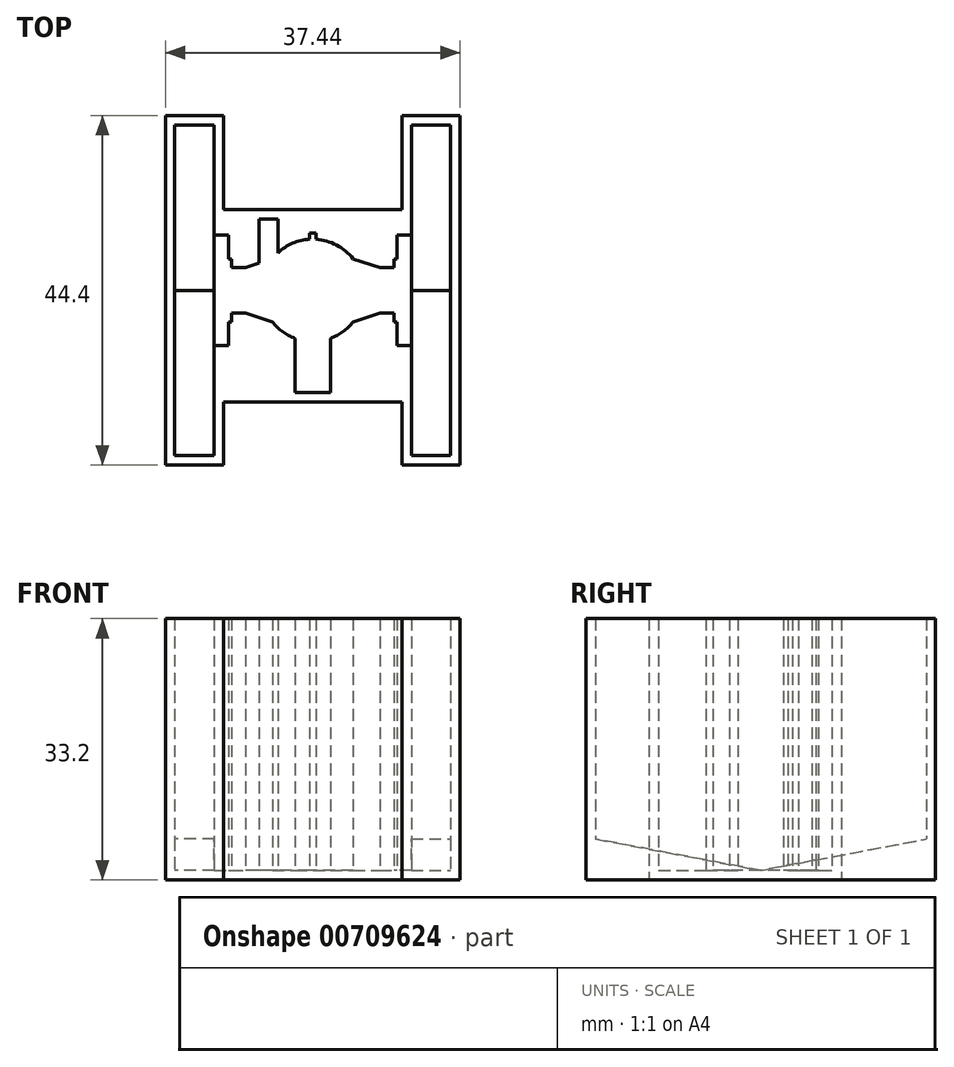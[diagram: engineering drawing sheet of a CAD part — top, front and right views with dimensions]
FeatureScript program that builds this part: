
annotation { "Feature Type Name" : "Feature", "Feature Type Description" : "" }
export const myFeature = defineFeature(function(context is Context, id is Id, definition is map)
    precondition{}
    {
        {
            var Q0;
            Q0=qCreatedBy(makeId("Top.planeOp"),FACE);
            var sketch = newSketch(context, id + "F0", { "sketchPlane" : qUnion([Q0])});
            skArc(sketch, "E0", {"start": v(-5.12, -4) * mm, "mid": v(-3.83, -5.25) * mm, "end": v(-2.25, -6.1) * mm});
            skLineSegment(sketch, "E1.bottom", {"start": v(12.52, 21) * mm, "end": v(12.52, 7) * mm});
            skLineSegment(sketch, "E1.left", {"start": v(12.52, 21) * mm, "end": v(17.52, 21) * mm});
            skLineSegment(sketch, "E1.right", {"start": v(12.52, -21) * mm, "end": v(17.52, -21) * mm});
            skLineSegment(sketch, "E2.left", {"start": v(8.52, 2.9) * mm, "end": v(10.32, 2.9) * mm});
            skLineSegment(sketch, "E3", {"start": v(8.52, 2.9) * mm, "end": v(8.52, 4) * mm, "construction": true});
            skLineSegment(sketch, "E4", {"start": v(8.52, 4) * mm, "end": v(5.12, 4) * mm, "construction": true});
            skLineSegment(sketch, "E5", {"start": v(5.12, 4) * mm, "end": v(8.52, 2.9) * mm});
            skLineSegment(sketch, "E6", {"start": v(17.52, 21) * mm, "end": v(17.52, 0) * mm});
            skLineSegment(sketch, "E7.MirrorCS", {"start": v(5.12, -4) * mm, "end": v(8.52, -2.9) * mm});
            skLineSegment(sketch, "E8.MirrorCS", {"start": v(8.52, -2.9) * mm, "end": v(10.32, -2.9) * mm});
            skLineSegment(sketch, "E9.MirrorCS", {"start": v(17.52, -21) * mm, "end": v(17.52, 0) * mm});
            skLineSegment(sketch, "E10", {"start": v(0, 29.44) * mm, "end": v(0, 7.3) * mm, "construction": true});
            skLineSegment(sketch, "E11.MirrorCS", {"start": v(-8.52, -2.9) * mm, "end": v(-10.32, -2.9) * mm});
            skLineSegment(sketch, "E12.MirrorCS", {"start": v(-12.52, -21) * mm, "end": v(-17.52, -21) * mm});
            skLineSegment(sketch, "E13.MirrorCS", {"start": v(-6.82, 3.45) * mm, "end": v(-8.52, 2.9) * mm});
            skLineSegment(sketch, "E14.MirrorCS", {"start": v(33.28, 0) * mm, "end": v(-32.9, 0) * mm, "construction": true});
            skLineSegment(sketch, "E15.MirrorCS", {"start": v(-5.12, -4) * mm, "end": v(-8.52, -2.9) * mm});
            skLineSegment(sketch, "E16.MirrorCS", {"start": v(-17.52, 21) * mm, "end": v(-17.52, 0) * mm});
            skLineSegment(sketch, "E17.MirrorCS", {"start": v(-12.52, 21) * mm, "end": v(-17.52, 21) * mm});
            skArc(sketch, "E18.MirrorC", {"start": v(-4.42, 4.76) * mm, "mid": v(-2.56, 5.97) * mm, "end": v(-0.4, 6.49) * mm});
            skLineSegment(sketch, "E19.MirrorCS", {"start": v(-17.52, -21) * mm, "end": v(-17.52, 0) * mm});
            skLineSegment(sketch, "E20", {"start": v(-6.82, 3.45) * mm, "end": v(-6.82, 9.06) * mm});
            skLineSegment(sketch, "E21", {"start": v(-4.42, 4.76) * mm, "end": v(-4.42, 9.06) * mm});
            skLineSegment(sketch, "E22", {"start": v(-4.42, 9.06) * mm, "end": v(-6.82, 9.06) * mm});
            skArc(sketch, "E23.trimOffspring", {"start": v(5.12, 4) * mm, "mid": v(3.03, 5.75) * mm, "end": v(0.4, 6.49) * mm});
            skArc(sketch, "E24.trimOffspring", {"start": v(5.12, -4) * mm, "mid": v(3.83, -5.25) * mm, "end": v(2.25, -6.1) * mm});
            skLineSegment(sketch, "E25", {"start": v(10.72, 4) * mm, "end": v(10.32, 4) * mm});
            skLineSegment(sketch, "E26", {"start": v(10.32, 4) * mm, "end": v(10.32, 2.9) * mm});
            skLineSegment(sketch, "E27.MirrorCS", {"start": v(10.32, -4) * mm, "end": v(10.32, -2.9) * mm});
            skLineSegment(sketch, "E28.MirrorCS", {"start": v(-10.32, 4) * mm, "end": v(-10.32, 2.9) * mm});
            skLineSegment(sketch, "E29.MirrorCS", {"start": v(-10.32, -4) * mm, "end": v(-10.32, -2.9) * mm});
            skLineSegment(sketch, "E30", {"start": v(-10.32, 2.9) * mm, "end": v(-8.52, 2.9) * mm});
            skLineSegment(sketch, "E31", {"start": v(0, 0) * mm, "end": v(0, -13) * mm, "construction": true});
            skLineSegment(sketch, "E32", {"start": v(-2.25, -13) * mm, "end": v(2.25, -13) * mm});
            skLineSegment(sketch, "E33", {"start": v(-2.25, -13) * mm, "end": v(-2.25, -6.1) * mm});
            skLineSegment(sketch, "E34", {"start": v(2.25, -13) * mm, "end": v(2.25, -6.1) * mm});
            skArc(sketch, "E35.trimOffspring", {"start": v(-2.25, -6.1) * mm, "mid": v(-3.83, -5.25) * mm, "end": v(-5.12, -4) * mm});
            skLineSegment(sketch, "E36", {"start": v(0, 7.3) * mm, "end": v(0.4, 7.3) * mm});
            skLineSegment(sketch, "E37", {"start": v(0.4, 7.3) * mm, "end": v(0.4, 6.49) * mm});
            skLineSegment(sketch, "E38", {"start": v(0, 7.3) * mm, "end": v(-0.4, 7.3) * mm});
            skLineSegment(sketch, "E39", {"start": v(-0.4, 7.3) * mm, "end": v(-0.4, 6.49) * mm});
            skLineSegment(sketch, "E40.trimOffspring", {"start": v(0, 6.5) * mm, "end": v(0, -27.69) * mm, "construction": true});
            skArc(sketch, "E41.trimOffspring", {"start": v(0.4, 6.49) * mm, "mid": v(3.03, 5.75) * mm, "end": v(5.12, 4) * mm});
            skArc(sketch, "E42.trimOffspring", {"start": v(-0.4, 6.49) * mm, "mid": v(-2.56, 5.97) * mm, "end": v(-4.42, 4.76) * mm});
            skLineSegment(sketch, "E43.MirrorCS", {"start": v(10.72, -4) * mm, "end": v(10.32, -4) * mm});
            skLineSegment(sketch, "E44.MirrorCS", {"start": v(-10.72, -4) * mm, "end": v(-10.32, -4) * mm});
            skLineSegment(sketch, "E45.MirrorCS", {"start": v(-10.72, 4) * mm, "end": v(-10.32, 4) * mm});
            skLineSegment(sketch, "E46", {"start": v(12.52, 7) * mm, "end": v(10.72, 7) * mm});
            skLineSegment(sketch, "E47", {"start": v(10.72, 7) * mm, "end": v(10.72, 4) * mm});
            skLineSegment(sketch, "E48.MirrorCS", {"start": v(12.52, -21) * mm, "end": v(12.52, -7) * mm});
            skLineSegment(sketch, "E49.MirrorCS", {"start": v(10.72, -7) * mm, "end": v(10.72, -4) * mm});
            skLineSegment(sketch, "E50.MirrorCS", {"start": v(12.52, -7) * mm, "end": v(10.72, -7) * mm});
            skLineSegment(sketch, "E51.MirrorCS", {"start": v(-12.52, -21) * mm, "end": v(-12.52, -7) * mm});
            skLineSegment(sketch, "E52.MirrorCS", {"start": v(-12.52, -7) * mm, "end": v(-10.72, -7) * mm});
            skLineSegment(sketch, "E53.MirrorCS", {"start": v(-10.72, -7) * mm, "end": v(-10.72, -4) * mm});
            skLineSegment(sketch, "E54.MirrorCS", {"start": v(-10.72, 7) * mm, "end": v(-10.72, 4) * mm});
            skLineSegment(sketch, "E55.MirrorCS", {"start": v(-12.52, 21) * mm, "end": v(-12.52, 7) * mm});
            skLineSegment(sketch, "E56.MirrorCS", {"start": v(-12.52, 7) * mm, "end": v(-10.72, 7) * mm});
            skArc(sketch, "E57", {"start": v(-19.07, 82.73) * mm, "mid": v(-17.82, 84.02) * mm, "end": v(-16.97, 85.6) * mm});
            skLineSegment(sketch, "E58.bottom", {"start": v(-44.07, 100.38) * mm, "end": v(-30.07, 100.38) * mm});
            skLineSegment(sketch, "E58.left", {"start": v(-44.07, 100.38) * mm, "end": v(-44.07, 105.38) * mm});
            skLineSegment(sketch, "E58.right", {"start": v(-2.07, 100.38) * mm, "end": v(-2.07, 105.38) * mm});
            skLineSegment(sketch, "E59.left", {"start": v(-25.97, 96.38) * mm, "end": v(-25.97, 98.18) * mm});
            skLineSegment(sketch, "E60", {"start": v(-25.97, 96.38) * mm, "end": v(-27.07, 96.38) * mm, "construction": true});
            skLineSegment(sketch, "E61", {"start": v(-27.07, 96.38) * mm, "end": v(-27.07, 92.98) * mm, "construction": true});
            skLineSegment(sketch, "E62", {"start": v(-27.07, 92.98) * mm, "end": v(-25.97, 96.38) * mm});
            skLineSegment(sketch, "E63", {"start": v(-44.07, 105.38) * mm, "end": v(-23.07, 105.38) * mm});
            skLineSegment(sketch, "E64.MirrorCS", {"start": v(-19.07, 92.98) * mm, "end": v(-20.17, 96.38) * mm});
            skLineSegment(sketch, "E65.MirrorCS", {"start": v(-20.17, 96.38) * mm, "end": v(-20.17, 98.18) * mm});
            skLineSegment(sketch, "E66.MirrorCS", {"start": v(-2.07, 105.38) * mm, "end": v(-23.07, 105.38) * mm});
            skLineSegment(sketch, "E67.MirrorCS", {"start": v(-20.17, 79.33) * mm, "end": v(-20.17, 77.53) * mm});
            skLineSegment(sketch, "E68.MirrorCS", {"start": v(-2.07, 75.33) * mm, "end": v(-2.07, 70.33) * mm});
            skLineSegment(sketch, "E69.MirrorCS", {"start": v(-26.52, 81.03) * mm, "end": v(-25.97, 79.33) * mm});
            skLineSegment(sketch, "E70.MirrorCS", {"start": v(-19.07, 82.73) * mm, "end": v(-20.17, 79.33) * mm});
            skLineSegment(sketch, "E71.MirrorCS", {"start": v(-44.07, 70.33) * mm, "end": v(-23.07, 70.33) * mm});
            skLineSegment(sketch, "E72.MirrorCS", {"start": v(-44.07, 75.33) * mm, "end": v(-44.07, 70.33) * mm});
            skArc(sketch, "E73.MirrorC", {"start": v(-27.83, 83.43) * mm, "mid": v(-29.04, 85.3) * mm, "end": v(-29.55, 87.45) * mm});
            skLineSegment(sketch, "E74.MirrorCS", {"start": v(-2.07, 70.33) * mm, "end": v(-23.07, 70.33) * mm});
            skLineSegment(sketch, "E75", {"start": v(-26.52, 81.03) * mm, "end": v(-32.13, 81.03) * mm});
            skLineSegment(sketch, "E76", {"start": v(-27.83, 83.43) * mm, "end": v(-32.13, 83.43) * mm});
            skLineSegment(sketch, "E77", {"start": v(-32.13, 83.43) * mm, "end": v(-32.13, 81.03) * mm});
            skArc(sketch, "E78.trimOffspring", {"start": v(-27.07, 92.98) * mm, "mid": v(-28.82, 90.88) * mm, "end": v(-29.55, 88.25) * mm});
            skArc(sketch, "E79.trimOffspring", {"start": v(-19.07, 92.98) * mm, "mid": v(-17.82, 91.69) * mm, "end": v(-16.97, 90.1) * mm});
            skLineSegment(sketch, "E80", {"start": v(-27.07, 98.58) * mm, "end": v(-27.07, 98.18) * mm});
            skLineSegment(sketch, "E81", {"start": v(-27.07, 98.18) * mm, "end": v(-25.97, 98.18) * mm});
            skLineSegment(sketch, "E82.MirrorCS", {"start": v(-19.07, 98.18) * mm, "end": v(-20.17, 98.18) * mm});
            skLineSegment(sketch, "E83.MirrorCS", {"start": v(-27.07, 77.53) * mm, "end": v(-25.97, 77.53) * mm});
            skLineSegment(sketch, "E84.MirrorCS", {"start": v(-19.07, 77.53) * mm, "end": v(-20.17, 77.53) * mm});
            skLineSegment(sketch, "E85", {"start": v(-25.97, 77.53) * mm, "end": v(-25.97, 79.33) * mm});
            skLineSegment(sketch, "E86", {"start": v(-23.07, 87.85) * mm, "end": v(-10.07, 87.85) * mm, "construction": true});
            skLineSegment(sketch, "E87", {"start": v(-10.07, 85.6) * mm, "end": v(-10.07, 90.1) * mm});
            skLineSegment(sketch, "E88", {"start": v(-10.07, 85.6) * mm, "end": v(-16.97, 85.6) * mm});
            skLineSegment(sketch, "E89", {"start": v(-10.07, 90.1) * mm, "end": v(-16.97, 90.1) * mm});
            skArc(sketch, "E90.trimOffspring", {"start": v(-16.97, 85.6) * mm, "mid": v(-17.82, 84.02) * mm, "end": v(-19.07, 82.73) * mm});
            skLineSegment(sketch, "E91", {"start": v(-30.37, 87.85) * mm, "end": v(-30.37, 88.25) * mm});
            skLineSegment(sketch, "E92", {"start": v(-30.37, 88.25) * mm, "end": v(-29.55, 88.25) * mm});
            skLineSegment(sketch, "E93", {"start": v(-30.37, 87.85) * mm, "end": v(-30.37, 87.45) * mm});
            skLineSegment(sketch, "E94", {"start": v(-30.37, 87.45) * mm, "end": v(-29.55, 87.45) * mm});
            skArc(sketch, "E95.trimOffspring", {"start": v(-29.55, 88.25) * mm, "mid": v(-28.82, 90.88) * mm, "end": v(-27.07, 92.98) * mm});
            skArc(sketch, "E96.trimOffspring", {"start": v(-29.55, 87.45) * mm, "mid": v(-29.04, 85.3) * mm, "end": v(-27.83, 83.43) * mm});
            skLineSegment(sketch, "E97.MirrorCS", {"start": v(-19.07, 98.58) * mm, "end": v(-19.07, 98.18) * mm});
            skLineSegment(sketch, "E98.MirrorCS", {"start": v(-19.07, 77.13) * mm, "end": v(-19.07, 77.53) * mm});
            skLineSegment(sketch, "E99.MirrorCS", {"start": v(-27.07, 77.13) * mm, "end": v(-27.07, 77.53) * mm});
            skLineSegment(sketch, "E100", {"start": v(-30.07, 100.38) * mm, "end": v(-30.07, 98.58) * mm});
            skLineSegment(sketch, "E101", {"start": v(-30.07, 98.58) * mm, "end": v(-27.07, 98.58) * mm});
            skLineSegment(sketch, "E102.MirrorCS", {"start": v(-2.07, 100.38) * mm, "end": v(-16.07, 100.38) * mm});
            skLineSegment(sketch, "E103.MirrorCS", {"start": v(-16.07, 98.58) * mm, "end": v(-19.07, 98.58) * mm});
            skLineSegment(sketch, "E104.MirrorCS", {"start": v(-16.07, 100.38) * mm, "end": v(-16.07, 98.58) * mm});
            skLineSegment(sketch, "E105.MirrorCS", {"start": v(-2.07, 75.33) * mm, "end": v(-16.07, 75.33) * mm});
            skLineSegment(sketch, "E106.MirrorCS", {"start": v(-16.07, 75.33) * mm, "end": v(-16.07, 77.13) * mm});
            skLineSegment(sketch, "E107.MirrorCS", {"start": v(-16.07, 77.13) * mm, "end": v(-19.07, 77.13) * mm});
            skLineSegment(sketch, "E108.MirrorCS", {"start": v(-30.07, 77.13) * mm, "end": v(-27.07, 77.13) * mm});
            skLineSegment(sketch, "E109.MirrorCS", {"start": v(-44.07, 75.33) * mm, "end": v(-30.07, 75.33) * mm});
            skLineSegment(sketch, "E110.MirrorCS", {"start": v(-30.07, 75.33) * mm, "end": v(-30.07, 77.13) * mm});
            skLineSegment(sketch, "E111.0", {"start": v(-11.32, -22.2) * mm, "end": v(-11.32, -14.2) * mm});
            skLineSegment(sketch, "E111.1", {"start": v(-11.32, -22.2) * mm, "end": v(-18.72, -22.2) * mm});
            skLineSegment(sketch, "E111.2", {"start": v(-11.32, 22.2) * mm, "end": v(-11.32, 10.26) * mm});
            skLineSegment(sketch, "E111.3", {"start": v(-11.32, 22.2) * mm, "end": v(-18.72, 22.2) * mm});
            skLineSegment(sketch, "E111.4", {"start": v(-18.72, 22.2) * mm, "end": v(-18.72, 0) * mm});
            skLineSegment(sketch, "E111.5", {"start": v(-18.72, -22.2) * mm, "end": v(-18.72, 0) * mm});
            skLineSegment(sketch, "E112.0", {"start": v(11.32, -22.2) * mm, "end": v(11.32, -14.2) * mm});
            skLineSegment(sketch, "E112.1", {"start": v(11.32, -22.2) * mm, "end": v(18.72, -22.2) * mm});
            skLineSegment(sketch, "E112.2", {"start": v(11.32, 22.2) * mm, "end": v(11.32, 10.26) * mm});
            skLineSegment(sketch, "E112.3", {"start": v(11.32, 22.2) * mm, "end": v(18.72, 22.2) * mm});
            skLineSegment(sketch, "E112.4", {"start": v(18.72, 22.2) * mm, "end": v(18.72, 0) * mm});
            skLineSegment(sketch, "E112.5", {"start": v(18.72, -22.2) * mm, "end": v(18.72, 0) * mm});
            skLineSegment(sketch, "E113.0", {"start": v(-4.42, 10.26) * mm, "end": v(-6.82, 10.26) * mm});
            skLineSegment(sketch, "E114.0", {"start": v(-2.25, -14.2) * mm, "end": v(2.25, -14.2) * mm});
            skLineSegment(sketch, "E115", {"start": v(-6.82, 10.26) * mm, "end": v(-11.32, 10.26) * mm});
            skLineSegment(sketch, "E116", {"start": v(-4.42, 10.26) * mm, "end": v(11.32, 10.26) * mm});
            skLineSegment(sketch, "E117", {"start": v(2.25, -14.2) * mm, "end": v(11.32, -14.2) * mm});
            skLineSegment(sketch, "E118", {"start": v(-2.25, -14.2) * mm, "end": v(-11.32, -14.2) * mm});
            skSolve(sketch);
        }
        {
            var Q0;
            Q0=makeQuery(id+"F0.imprint","IMPRINT",FACE,{"disambiguationData":[TD([[makeQuery(id+"F0.imprint","IMPRINT",EDGE,{"derivedFrom":sQuery(id+"F0.wireOp",EDGE,"E1.bottom")}),-1.0]])]});
            extrude(context, id + "F1", {"entities" : qUnion([Q0]), "depth" : 32 * mm, "offsetDistance" : 25 * mm});
        }
        {
            var Q0;
            Q0=makeQuery(id+"F1.opExtrude","CAP_FACE",FACE,{"disambiguationData":[OSD([sQuery(id+"F0.wireOp",EDGE,"E1.bottom"),sQuery(id+"F0.wireOp",EDGE,"E1.left"),sQuery(id+"F0.wireOp",EDGE,"E2.left"),sQuery(id+"F0.wireOp",EDGE,"E5"),sQuery(id+"F0.wireOp",EDGE,"E6"),sQuery(id+"F0.wireOp",EDGE,"E7.MirrorCS"),sQuery(id+"F0.wireOp",EDGE,"E8.MirrorCS"),sQuery(id+"F0.wireOp",EDGE,"E9.MirrorCS"),sQuery(id+"F0.wireOp",EDGE,"E1.right"),sQuery(id+"F0.wireOp",EDGE,"E11.MirrorCS"),sQuery(id+"F0.wireOp",EDGE,"E13.MirrorCS"),sQuery(id+"F0.wireOp",EDGE,"E15.MirrorCS"),sQuery(id+"F0.wireOp",EDGE,"E16.MirrorCS"),sQuery(id+"F0.wireOp",EDGE,"E12.MirrorCS"),sQuery(id+"F0.wireOp",EDGE,"E17.MirrorCS"),sQuery(id+"F0.wireOp",EDGE,"E19.MirrorCS"),sQuery(id+"F0.wireOp",EDGE,"E20"),sQuery(id+"F0.wireOp",EDGE,"E21"),sQuery(id+"F0.wireOp",EDGE,"E22"),sQuery(id+"F0.wireOp",EDGE,"E24.trimOffspring"),sQuery(id+"F0.wireOp",EDGE,"E25"),sQuery(id+"F0.wireOp",EDGE,"E26"),sQuery(id+"F0.wireOp",EDGE,"E27.MirrorCS"),sQuery(id+"F0.wireOp",EDGE,"E28.MirrorCS"),sQuery(id+"F0.wireOp",EDGE,"E29.MirrorCS"),sQuery(id+"F0.wireOp",EDGE,"E30"),sQuery(id+"F0.wireOp",EDGE,"E32"),sQuery(id+"F0.wireOp",EDGE,"E33"),sQuery(id+"F0.wireOp",EDGE,"E34"),sQuery(id+"F0.wireOp",EDGE,"E35.trimOffspring"),sQuery(id+"F0.wireOp",EDGE,"E36"),sQuery(id+"F0.wireOp",EDGE,"E37"),sQuery(id+"F0.wireOp",EDGE,"E38"),sQuery(id+"F0.wireOp",EDGE,"E39"),sQuery(id+"F0.wireOp",EDGE,"E41.trimOffspring"),sQuery(id+"F0.wireOp",EDGE,"E42.trimOffspring"),sQuery(id+"F0.wireOp",EDGE,"E43.MirrorCS"),sQuery(id+"F0.wireOp",EDGE,"E44.MirrorCS"),sQuery(id+"F0.wireOp",EDGE,"E45.MirrorCS"),sQuery(id+"F0.wireOp",EDGE,"E46"),sQuery(id+"F0.wireOp",EDGE,"E47"),sQuery(id+"F0.wireOp",EDGE,"E48.MirrorCS"),sQuery(id+"F0.wireOp",EDGE,"E49.MirrorCS"),sQuery(id+"F0.wireOp",EDGE,"E50.MirrorCS"),sQuery(id+"F0.wireOp",EDGE,"E51.MirrorCS"),sQuery(id+"F0.wireOp",EDGE,"E52.MirrorCS"),sQuery(id+"F0.wireOp",EDGE,"E53.MirrorCS"),sQuery(id+"F0.wireOp",EDGE,"E54.MirrorCS"),sQuery(id+"F0.wireOp",EDGE,"E55.MirrorCS"),sQuery(id+"F0.wireOp",EDGE,"E56.MirrorCS"),sQuery(id+"F0.wireOp",EDGE,"E111.0"),sQuery(id+"F0.wireOp",EDGE,"E111.1"),sQuery(id+"F0.wireOp",EDGE,"E111.2"),sQuery(id+"F0.wireOp",EDGE,"E111.3"),sQuery(id+"F0.wireOp",EDGE,"E111.4"),sQuery(id+"F0.wireOp",EDGE,"E111.5"),sQuery(id+"F0.wireOp",EDGE,"E112.0"),sQuery(id+"F0.wireOp",EDGE,"E112.1"),sQuery(id+"F0.wireOp",EDGE,"E112.2"),sQuery(id+"F0.wireOp",EDGE,"E112.3"),sQuery(id+"F0.wireOp",EDGE,"E112.4"),sQuery(id+"F0.wireOp",EDGE,"E112.5"),sQuery(id+"F0.wireOp",EDGE,"E113.0"),sQuery(id+"F0.wireOp",EDGE,"E114.0"),sQuery(id+"F0.wireOp",EDGE,"E115"),sQuery(id+"F0.wireOp",EDGE,"E116"),sQuery(id+"F0.wireOp",EDGE,"E117"),sQuery(id+"F0.wireOp",EDGE,"E118")])],"isStart":true});
            var sketch = newSketch(context, id + "F2", { "sketchPlane" : qUnion([Q0])});
            skLineSegment(sketch, "E119.0", {"start": v(11.32, -22.2) * mm, "end": v(11.32, -10.26) * mm});
            skLineSegment(sketch, "E119.1", {"start": v(11.32, -22.2) * mm, "end": v(18.72, -22.2) * mm});
            skLineSegment(sketch, "E119.2", {"start": v(18.72, 22.2) * mm, "end": v(18.72, -22.2) * mm});
            skLineSegment(sketch, "E119.3", {"start": v(-11.32, -10.26) * mm, "end": v(11.32, -10.26) * mm});
            skLineSegment(sketch, "E119.4", {"start": v(-11.32, -22.2) * mm, "end": v(-11.32, -10.26) * mm});
            skLineSegment(sketch, "E119.5", {"start": v(-11.32, -22.2) * mm, "end": v(-18.72, -22.2) * mm});
            skLineSegment(sketch, "E119.6", {"start": v(-18.72, -22.2) * mm, "end": v(-18.72, 22.2) * mm});
            skLineSegment(sketch, "E119.7", {"start": v(11.32, 22.2) * mm, "end": v(18.72, 22.2) * mm});
            skLineSegment(sketch, "E119.8", {"start": v(11.32, 22.2) * mm, "end": v(11.32, 14.2) * mm});
            skLineSegment(sketch, "E119.9", {"start": v(11.32, 14.2) * mm, "end": v(-11.32, 14.2) * mm});
            skLineSegment(sketch, "E119.10", {"start": v(-11.32, 22.2) * mm, "end": v(-11.32, 14.2) * mm});
            skLineSegment(sketch, "E119.11", {"start": v(-11.32, 22.2) * mm, "end": v(-18.72, 22.2) * mm});
            skLineSegment(sketch, "E120", {"start": v(18.72, 0) * mm, "end": v(-17.52, 0) * mm});
            skSolve(sketch);
        }
        {
            var Q0;
            Q0=makeQuery(id+"F2.imprint","IMPRINT",FACE,{"disambiguationData":[TD([[makeQuery(id+"F2.imprint","IMPRINT",EDGE,{"derivedFrom":sQuery(id+"F2.wireOp",EDGE,"E119.0")}),-1.0]])]});
            var Q1;
            Q1=makeQuery(id+"F2.imprint","IMPRINT",FACE,{"disambiguationData":[TD([[makeQuery(id+"F2.imprint","IMPRINT",EDGE,{"derivedFrom":makeQuery(id+"F1.opExtrude","CAP_EDGE",EDGE,{"disambiguationData":[OSD([sQuery(id+"F0.wireOp",EDGE,"E1.bottom")])],"isStart":true})}),-1.0]])]});
            var Q2;
            Q2=makeQuery(id+"F2.imprint","IMPRINT",FACE,{"disambiguationData":[TD([[makeQuery(id+"F2.imprint","IMPRINT",EDGE,{"derivedFrom":makeQuery(id+"F1.opExtrude","CAP_EDGE",EDGE,{"disambiguationData":[OSD([sQuery(id+"F0.wireOp",EDGE,"E7.MirrorCS")])],"isStart":true})}),-1.0]])]});
            extrude(context, id + "F3", {"entities" : qUnion([Q0, Q1, Q2]), "operationType" : NewBodyOperationType.ADD, "depth" : 1.2 * mm, "offsetDistance" : 25 * mm});
        }
        {
            var Q0;
            Q0=makeQuery(id+"F3.opExtrude","CAP_FACE",FACE,{"disambiguationData":[OSD([sQuery(id+"F2.wireOp",EDGE,"E119.0"),sQuery(id+"F2.wireOp",EDGE,"E119.1"),sQuery(id+"F2.wireOp",EDGE,"E119.2"),sQuery(id+"F2.wireOp",EDGE,"E119.3"),sQuery(id+"F2.wireOp",EDGE,"E119.4"),sQuery(id+"F2.wireOp",EDGE,"E119.5"),sQuery(id+"F2.wireOp",EDGE,"E119.6"),sQuery(id+"F2.wireOp",EDGE,"E119.7"),sQuery(id+"F2.wireOp",EDGE,"E119.8"),sQuery(id+"F2.wireOp",EDGE,"E119.9"),sQuery(id+"F2.wireOp",EDGE,"E119.10"),sQuery(id+"F2.wireOp",EDGE,"E119.11")])],"isStart":true});
            var sketch = newSketch(context, id + "F4", { "sketchPlane" : qUnion([Q0])});
            skLineSegment(sketch, "E121.0", {"start": v(17.52, 21) * mm, "end": v(17.52, -21) * mm});
            skLineSegment(sketch, "E121.1", {"start": v(12.52, 21) * mm, "end": v(17.52, 21) * mm});
            skLineSegment(sketch, "E121.2", {"start": v(12.52, 21) * mm, "end": v(12.52, 7) * mm});
            skLineSegment(sketch, "E121.3", {"start": v(12.52, -21) * mm, "end": v(12.52, -7) * mm});
            skLineSegment(sketch, "E121.4", {"start": v(12.52, -21) * mm, "end": v(17.52, -21) * mm});
            skLineSegment(sketch, "E121.5", {"start": v(-17.52, -21) * mm, "end": v(-17.52, 21) * mm});
            skLineSegment(sketch, "E121.6", {"start": v(-12.52, 21) * mm, "end": v(-17.52, 21) * mm});
            skLineSegment(sketch, "E121.7", {"start": v(-12.52, 21) * mm, "end": v(-12.52, 7) * mm});
            skLineSegment(sketch, "E121.8", {"start": v(-12.52, -21) * mm, "end": v(-17.52, -21) * mm});
            skLineSegment(sketch, "E121.9", {"start": v(-12.52, -21) * mm, "end": v(-12.52, -7) * mm});
            skLineSegment(sketch, "E122", {"start": v(-12.52, 7) * mm, "end": v(-12.52, -7) * mm});
            skLineSegment(sketch, "E123", {"start": v(12.52, 7) * mm, "end": v(12.52, -7) * mm});
            skLineSegment(sketch, "E124", {"start": v(12.52, 0) * mm, "end": v(17.52, 0) * mm});
            skLineSegment(sketch, "E125", {"start": v(-12.52, 0) * mm, "end": v(-17.52, 0) * mm});
            skSolve(sketch);
        }
        {
            var Q0;
            Q0=makeQuery(id+"F1.opExtrude","SWEPT_FACE",FACE,{"disambiguationData":[OSD([sQuery(id+"F0.wireOp",EDGE,"E16.MirrorCS"),sQuery(id+"F0.wireOp",EDGE,"E19.MirrorCS")])]});
            var sketch = newSketch(context, id + "F5", { "sketchPlane" : qUnion([Q0])});
            skPoint(sketch, "E126.0", {"position": v(21, 0) * mm});
            skLineSegment(sketch, "E126.1", {"start": v(-21, 0) * mm, "end": v(21, 0) * mm});
            skLineSegment(sketch, "E126.2", {"start": v(-21, 4) * mm, "end": v(-21, 0) * mm});
            skLineSegment(sketch, "E127", {"start": v(21, 0) * mm, "end": v(21, 4) * mm});
            skLineSegment(sketch, "E128", {"start": v(21, 4) * mm, "end": v(0, 0) * mm});
            skLineSegment(sketch, "E129", {"start": v(0, 0) * mm, "end": v(-21, 4) * mm});
            skPoint(sketch, "E130.orphan", {"position": v(-21, 32) * mm});
            skSolve(sketch);
        }
        {
            var Q0;
            Q0=makeQuery(id+"F1.opExtrude","SWEPT_FACE",FACE,{"disambiguationData":[OSD([sQuery(id+"F0.wireOp",EDGE,"E6"),sQuery(id+"F0.wireOp",EDGE,"E9.MirrorCS")])]});
            var sketch = newSketch(context, id + "F6", { "sketchPlane" : qUnion([Q0])});
            skLineSegment(sketch, "E131.0", {"start": v(-21, 0) * mm, "end": v(21, 0) * mm});
            skPoint(sketch, "E132.0", {"position": v(0, 0) * mm});
            skLineSegment(sketch, "E133", {"start": v(21, 0) * mm, "end": v(21, 4) * mm});
            skLineSegment(sketch, "E134", {"start": v(21, 4) * mm, "end": v(0, 0) * mm});
            skLineSegment(sketch, "E135", {"start": v(0, 0) * mm, "end": v(-21, 4) * mm});
            skLineSegment(sketch, "E136", {"start": v(-21, 4) * mm, "end": v(-21, 0) * mm});
            skSolve(sketch);
        }
        {
            var Q0;
            Q0 = qSketchRegion(id + "F5", true);
            var Q1;
            Q1=sQuery(id+"F4.wireOp",VERTEX,"E121.9.end");
            extrude(context, id + "F7", {"entities" : qUnion([Q0]), "operationType" : NewBodyOperationType.ADD, "endBound" : BoundingType.UP_TO_VERTEX, "depth" : 25 * mm, "endBoundEntityVertex" : qUnion([Q1]), "offsetDistance" : 25 * mm});
        }
        {
            var Q0;
            Q0 = qSketchRegion(id + "F6", true);
            var Q1;
            Q1=makeQuery(id+"F1.opExtrude","CAP_VERTEX",VERTEX,{"disambiguationData":[OSD([sQuery(id+"F0.wireOp",EDGE,"E1.bottom"),sQuery(id+"F0.wireOp",EDGE,"E46")])],"isStart":true});
            extrude(context, id + "F8", {"entities" : qUnion([Q0]), "operationType" : NewBodyOperationType.ADD, "endBound" : BoundingType.UP_TO_VERTEX, "depth" : 25 * mm, "endBoundEntityVertex" : qUnion([Q1]), "offsetDistance" : 25 * mm});
        }
    });
